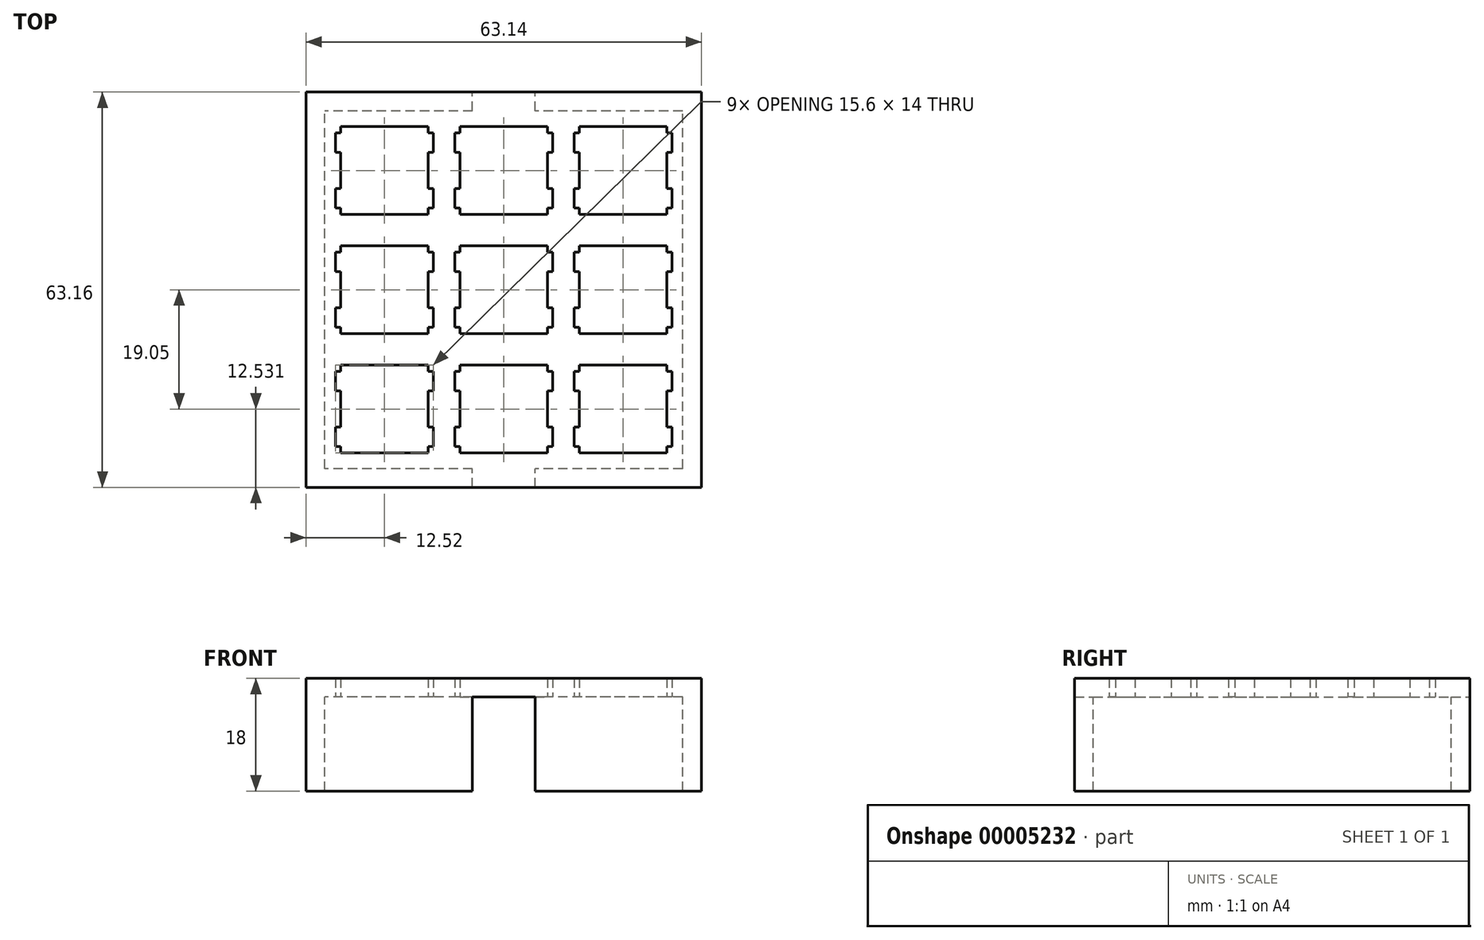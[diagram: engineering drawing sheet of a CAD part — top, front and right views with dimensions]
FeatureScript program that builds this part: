
annotation { "Feature Type Name" : "Feature", "Feature Type Description" : "" }
export const myFeature = defineFeature(function(context is Context, id is Id, definition is map)
    precondition{}
    {
        {
            var Q0;
            Q0=qCreatedBy(makeId("Top.planeOp"),FACE);
            var sketch = newSketch(context, id + "F0", { "sketchPlane" : qUnion([Q0])});
            skLineSegment(sketch, "E0", {"start": v(-31.57, 31.58) * mm, "end": v(31.57, 31.58) * mm});
            skLineSegment(sketch, "E1", {"start": v(31.57, 31.58) * mm, "end": v(31.57, -31.58) * mm});
            skLineSegment(sketch, "E2", {"start": v(31.57, -31.58) * mm, "end": v(-31.57, -31.58) * mm});
            skLineSegment(sketch, "E3", {"start": v(-31.57, -31.58) * mm, "end": v(-31.57, 31.58) * mm});
            skLineSegment(sketch, "E4", {"start": v(-12.05, 13.05) * mm, "end": v(-12.05, 12.05) * mm});
            skLineSegment(sketch, "E5", {"start": v(-12.05, 12.05) * mm, "end": v(-26.05, 12.05) * mm});
            skLineSegment(sketch, "E6", {"start": v(-26.05, 12.05) * mm, "end": v(-26.05, 13.05) * mm});
            skLineSegment(sketch, "E7", {"start": v(-26.05, 13.05) * mm, "end": v(-26.85, 13.05) * mm});
            skLineSegment(sketch, "E8", {"start": v(-26.85, 13.05) * mm, "end": v(-26.85, 16.15) * mm});
            skLineSegment(sketch, "E9", {"start": v(-26.85, 16.15) * mm, "end": v(-26.05, 16.15) * mm});
            skLineSegment(sketch, "E10", {"start": v(-26.05, 16.15) * mm, "end": v(-26.05, 21.95) * mm});
            skLineSegment(sketch, "E11", {"start": v(-26.05, 21.95) * mm, "end": v(-26.85, 21.95) * mm});
            skLineSegment(sketch, "E12", {"start": v(-26.85, 21.95) * mm, "end": v(-26.85, 25.05) * mm});
            skLineSegment(sketch, "E13", {"start": v(-26.85, 25.05) * mm, "end": v(-26.05, 25.05) * mm});
            skLineSegment(sketch, "E14", {"start": v(-26.05, 25.05) * mm, "end": v(-26.05, 26.05) * mm});
            skLineSegment(sketch, "E15", {"start": v(-26.05, 26.05) * mm, "end": v(-12.05, 26.05) * mm});
            skLineSegment(sketch, "E16", {"start": v(-12.05, 26.05) * mm, "end": v(-12.05, 25.05) * mm});
            skLineSegment(sketch, "E17", {"start": v(-12.05, 25.05) * mm, "end": v(-11.25, 25.05) * mm});
            skLineSegment(sketch, "E18", {"start": v(-11.25, 25.05) * mm, "end": v(-11.25, 21.95) * mm});
            skLineSegment(sketch, "E19", {"start": v(-11.25, 21.95) * mm, "end": v(-12.05, 21.95) * mm});
            skLineSegment(sketch, "E20", {"start": v(-12.05, 21.95) * mm, "end": v(-12.05, 16.15) * mm});
            skLineSegment(sketch, "E21", {"start": v(-12.05, 16.15) * mm, "end": v(-11.25, 16.15) * mm});
            skLineSegment(sketch, "E22", {"start": v(-11.25, 16.15) * mm, "end": v(-11.25, 13.05) * mm});
            skLineSegment(sketch, "E23", {"start": v(-11.25, 13.05) * mm, "end": v(-12.05, 13.05) * mm});
            skLineSegment(sketch, "E24", {"start": v(-12.05, -6) * mm, "end": v(-12.05, -7) * mm});
            skLineSegment(sketch, "E25", {"start": v(-12.05, -7) * mm, "end": v(-26.05, -7) * mm});
            skLineSegment(sketch, "E26", {"start": v(-26.05, -7) * mm, "end": v(-26.05, -6) * mm});
            skLineSegment(sketch, "E27", {"start": v(-26.05, -6) * mm, "end": v(-26.85, -6) * mm});
            skLineSegment(sketch, "E28", {"start": v(-26.85, -6) * mm, "end": v(-26.85, -2.9) * mm});
            skLineSegment(sketch, "E29", {"start": v(-26.85, -2.9) * mm, "end": v(-26.05, -2.9) * mm});
            skLineSegment(sketch, "E30", {"start": v(-26.05, -2.9) * mm, "end": v(-26.05, 2.9) * mm});
            skLineSegment(sketch, "E31", {"start": v(-26.05, 2.9) * mm, "end": v(-26.85, 2.9) * mm});
            skLineSegment(sketch, "E32", {"start": v(-26.85, 2.9) * mm, "end": v(-26.85, 6) * mm});
            skLineSegment(sketch, "E33", {"start": v(-26.85, 6) * mm, "end": v(-26.05, 6) * mm});
            skLineSegment(sketch, "E34", {"start": v(-26.05, 6) * mm, "end": v(-26.05, 7) * mm});
            skLineSegment(sketch, "E35", {"start": v(-26.05, 7) * mm, "end": v(-12.05, 7) * mm});
            skLineSegment(sketch, "E36", {"start": v(-12.05, 7) * mm, "end": v(-12.05, 6) * mm});
            skLineSegment(sketch, "E37", {"start": v(-12.05, 6) * mm, "end": v(-11.25, 6) * mm});
            skLineSegment(sketch, "E38", {"start": v(-11.25, 6) * mm, "end": v(-11.25, 2.9) * mm});
            skLineSegment(sketch, "E39", {"start": v(-11.25, 2.9) * mm, "end": v(-12.05, 2.9) * mm});
            skLineSegment(sketch, "E40", {"start": v(-12.05, 2.9) * mm, "end": v(-12.05, -2.9) * mm});
            skLineSegment(sketch, "E41", {"start": v(-12.05, -2.9) * mm, "end": v(-11.25, -2.9) * mm});
            skLineSegment(sketch, "E42", {"start": v(-11.25, -2.9) * mm, "end": v(-11.25, -6) * mm});
            skLineSegment(sketch, "E43", {"start": v(-11.25, -6) * mm, "end": v(-12.05, -6) * mm});
            skLineSegment(sketch, "E44", {"start": v(-12.05, -25.05) * mm, "end": v(-12.05, -26.05) * mm});
            skLineSegment(sketch, "E45", {"start": v(-12.05, -26.05) * mm, "end": v(-26.05, -26.05) * mm});
            skLineSegment(sketch, "E46", {"start": v(-26.05, -26.05) * mm, "end": v(-26.05, -25.05) * mm});
            skLineSegment(sketch, "E47", {"start": v(-26.05, -25.05) * mm, "end": v(-26.85, -25.05) * mm});
            skLineSegment(sketch, "E48", {"start": v(-26.85, -25.05) * mm, "end": v(-26.85, -21.95) * mm});
            skLineSegment(sketch, "E49", {"start": v(-26.85, -21.95) * mm, "end": v(-26.05, -21.95) * mm});
            skLineSegment(sketch, "E50", {"start": v(-26.05, -21.95) * mm, "end": v(-26.05, -16.15) * mm});
            skLineSegment(sketch, "E51", {"start": v(-26.05, -16.15) * mm, "end": v(-26.85, -16.15) * mm});
            skLineSegment(sketch, "E52", {"start": v(-26.85, -16.15) * mm, "end": v(-26.85, -13.05) * mm});
            skLineSegment(sketch, "E53", {"start": v(-26.85, -13.05) * mm, "end": v(-26.05, -13.05) * mm});
            skLineSegment(sketch, "E54", {"start": v(-26.05, -13.05) * mm, "end": v(-26.05, -12.05) * mm});
            skLineSegment(sketch, "E55", {"start": v(-26.05, -12.05) * mm, "end": v(-12.05, -12.05) * mm});
            skLineSegment(sketch, "E56", {"start": v(-12.05, -12.05) * mm, "end": v(-12.05, -13.05) * mm});
            skLineSegment(sketch, "E57", {"start": v(-12.05, -13.05) * mm, "end": v(-11.25, -13.05) * mm});
            skLineSegment(sketch, "E58", {"start": v(-11.25, -13.05) * mm, "end": v(-11.25, -16.15) * mm});
            skLineSegment(sketch, "E59", {"start": v(-11.25, -16.15) * mm, "end": v(-12.05, -16.15) * mm});
            skLineSegment(sketch, "E60", {"start": v(-12.05, -16.15) * mm, "end": v(-12.05, -21.95) * mm});
            skLineSegment(sketch, "E61", {"start": v(-12.05, -21.95) * mm, "end": v(-11.25, -21.95) * mm});
            skLineSegment(sketch, "E62", {"start": v(-11.25, -21.95) * mm, "end": v(-11.25, -25.05) * mm});
            skLineSegment(sketch, "E63", {"start": v(-11.25, -25.05) * mm, "end": v(-12.05, -25.05) * mm});
            skLineSegment(sketch, "E64", {"start": v(7, 13.05) * mm, "end": v(7, 12.05) * mm});
            skLineSegment(sketch, "E65", {"start": v(7, 12.05) * mm, "end": v(-7, 12.05) * mm});
            skLineSegment(sketch, "E66", {"start": v(-7, 12.05) * mm, "end": v(-7, 13.05) * mm});
            skLineSegment(sketch, "E67", {"start": v(-7, 13.05) * mm, "end": v(-7.8, 13.05) * mm});
            skLineSegment(sketch, "E68", {"start": v(-7.8, 13.05) * mm, "end": v(-7.8, 16.15) * mm});
            skLineSegment(sketch, "E69", {"start": v(-7.8, 16.15) * mm, "end": v(-7, 16.15) * mm});
            skLineSegment(sketch, "E70", {"start": v(-7, 16.15) * mm, "end": v(-7, 21.95) * mm});
            skLineSegment(sketch, "E71", {"start": v(-7, 21.95) * mm, "end": v(-7.8, 21.95) * mm});
            skLineSegment(sketch, "E72", {"start": v(-7.8, 21.95) * mm, "end": v(-7.8, 25.05) * mm});
            skLineSegment(sketch, "E73", {"start": v(-7.8, 25.05) * mm, "end": v(-7, 25.05) * mm});
            skLineSegment(sketch, "E74", {"start": v(-7, 25.05) * mm, "end": v(-7, 26.05) * mm});
            skLineSegment(sketch, "E75", {"start": v(-7, 26.05) * mm, "end": v(7, 26.05) * mm});
            skLineSegment(sketch, "E76", {"start": v(7, 26.05) * mm, "end": v(7, 25.05) * mm});
            skLineSegment(sketch, "E77", {"start": v(7, 25.05) * mm, "end": v(7.8, 25.05) * mm});
            skLineSegment(sketch, "E78", {"start": v(7.8, 25.05) * mm, "end": v(7.8, 21.95) * mm});
            skLineSegment(sketch, "E79", {"start": v(7.8, 21.95) * mm, "end": v(7, 21.95) * mm});
            skLineSegment(sketch, "E80", {"start": v(7, 21.95) * mm, "end": v(7, 16.15) * mm});
            skLineSegment(sketch, "E81", {"start": v(7, 16.15) * mm, "end": v(7.8, 16.15) * mm});
            skLineSegment(sketch, "E82", {"start": v(7.8, 16.15) * mm, "end": v(7.8, 13.05) * mm});
            skLineSegment(sketch, "E83", {"start": v(7.8, 13.05) * mm, "end": v(7, 13.05) * mm});
            skLineSegment(sketch, "E84", {"start": v(7, -6) * mm, "end": v(7, -7) * mm});
            skLineSegment(sketch, "E85", {"start": v(7, -7) * mm, "end": v(-7, -7) * mm});
            skLineSegment(sketch, "E86", {"start": v(-7, -7) * mm, "end": v(-7, -6) * mm});
            skLineSegment(sketch, "E87", {"start": v(-7, -6) * mm, "end": v(-7.8, -6) * mm});
            skLineSegment(sketch, "E88", {"start": v(-7.8, -6) * mm, "end": v(-7.8, -2.9) * mm});
            skLineSegment(sketch, "E89", {"start": v(-7.8, -2.9) * mm, "end": v(-7, -2.9) * mm});
            skLineSegment(sketch, "E90", {"start": v(-7, -2.9) * mm, "end": v(-7, 2.9) * mm});
            skLineSegment(sketch, "E91", {"start": v(-7, 2.9) * mm, "end": v(-7.8, 2.9) * mm});
            skLineSegment(sketch, "E92", {"start": v(-7.8, 2.9) * mm, "end": v(-7.8, 6) * mm});
            skLineSegment(sketch, "E93", {"start": v(-7.8, 6) * mm, "end": v(-7, 6) * mm});
            skLineSegment(sketch, "E94", {"start": v(-7, 6) * mm, "end": v(-7, 7) * mm});
            skLineSegment(sketch, "E95", {"start": v(-7, 7) * mm, "end": v(7, 7) * mm});
            skLineSegment(sketch, "E96", {"start": v(7, 7) * mm, "end": v(7, 6) * mm});
            skLineSegment(sketch, "E97", {"start": v(7, 6) * mm, "end": v(7.8, 6) * mm});
            skLineSegment(sketch, "E98", {"start": v(7.8, 6) * mm, "end": v(7.8, 2.9) * mm});
            skLineSegment(sketch, "E99", {"start": v(7.8, 2.9) * mm, "end": v(7, 2.9) * mm});
            skLineSegment(sketch, "E100", {"start": v(7, 2.9) * mm, "end": v(7, -2.9) * mm});
            skLineSegment(sketch, "E101", {"start": v(7, -2.9) * mm, "end": v(7.8, -2.9) * mm});
            skLineSegment(sketch, "E102", {"start": v(7.8, -2.9) * mm, "end": v(7.8, -6) * mm});
            skLineSegment(sketch, "E103", {"start": v(7.8, -6) * mm, "end": v(7, -6) * mm});
            skLineSegment(sketch, "E104", {"start": v(7, -25.05) * mm, "end": v(7, -26.05) * mm});
            skLineSegment(sketch, "E105", {"start": v(7, -26.05) * mm, "end": v(-7, -26.05) * mm});
            skLineSegment(sketch, "E106", {"start": v(-7, -26.05) * mm, "end": v(-7, -25.05) * mm});
            skLineSegment(sketch, "E107", {"start": v(-7, -25.05) * mm, "end": v(-7.8, -25.05) * mm});
            skLineSegment(sketch, "E108", {"start": v(-7.8, -25.05) * mm, "end": v(-7.8, -21.95) * mm});
            skLineSegment(sketch, "E109", {"start": v(-7.8, -21.95) * mm, "end": v(-7, -21.95) * mm});
            skLineSegment(sketch, "E110", {"start": v(-7, -21.95) * mm, "end": v(-7, -16.15) * mm});
            skLineSegment(sketch, "E111", {"start": v(-7, -16.15) * mm, "end": v(-7.8, -16.15) * mm});
            skLineSegment(sketch, "E112", {"start": v(-7.8, -16.15) * mm, "end": v(-7.8, -13.05) * mm});
            skLineSegment(sketch, "E113", {"start": v(-7.8, -13.05) * mm, "end": v(-7, -13.05) * mm});
            skLineSegment(sketch, "E114", {"start": v(-7, -13.05) * mm, "end": v(-7, -12.05) * mm});
            skLineSegment(sketch, "E115", {"start": v(-7, -12.05) * mm, "end": v(7, -12.05) * mm});
            skLineSegment(sketch, "E116", {"start": v(7, -12.05) * mm, "end": v(7, -13.05) * mm});
            skLineSegment(sketch, "E117", {"start": v(7, -13.05) * mm, "end": v(7.8, -13.05) * mm});
            skLineSegment(sketch, "E118", {"start": v(7.8, -13.05) * mm, "end": v(7.8, -16.15) * mm});
            skLineSegment(sketch, "E119", {"start": v(7.8, -16.15) * mm, "end": v(7, -16.15) * mm});
            skLineSegment(sketch, "E120", {"start": v(7, -16.15) * mm, "end": v(7, -21.95) * mm});
            skLineSegment(sketch, "E121", {"start": v(7, -21.95) * mm, "end": v(7.8, -21.95) * mm});
            skLineSegment(sketch, "E122", {"start": v(7.8, -21.95) * mm, "end": v(7.8, -25.05) * mm});
            skLineSegment(sketch, "E123", {"start": v(7.8, -25.05) * mm, "end": v(7, -25.05) * mm});
            skLineSegment(sketch, "E124", {"start": v(26.05, 13.05) * mm, "end": v(26.05, 12.05) * mm});
            skLineSegment(sketch, "E125", {"start": v(26.05, 12.05) * mm, "end": v(12.05, 12.05) * mm});
            skLineSegment(sketch, "E126", {"start": v(12.05, 12.05) * mm, "end": v(12.05, 13.05) * mm});
            skLineSegment(sketch, "E127", {"start": v(12.05, 13.05) * mm, "end": v(11.25, 13.05) * mm});
            skLineSegment(sketch, "E128", {"start": v(11.25, 13.05) * mm, "end": v(11.25, 16.15) * mm});
            skLineSegment(sketch, "E129", {"start": v(11.25, 16.15) * mm, "end": v(12.05, 16.15) * mm});
            skLineSegment(sketch, "E130", {"start": v(12.05, 16.15) * mm, "end": v(12.05, 21.95) * mm});
            skLineSegment(sketch, "E131", {"start": v(12.05, 21.95) * mm, "end": v(11.25, 21.95) * mm});
            skLineSegment(sketch, "E132", {"start": v(11.25, 21.95) * mm, "end": v(11.25, 25.05) * mm});
            skLineSegment(sketch, "E133", {"start": v(11.25, 25.05) * mm, "end": v(12.05, 25.05) * mm});
            skLineSegment(sketch, "E134", {"start": v(12.05, 25.05) * mm, "end": v(12.05, 26.05) * mm});
            skLineSegment(sketch, "E135", {"start": v(12.05, 26.05) * mm, "end": v(26.05, 26.05) * mm});
            skLineSegment(sketch, "E136", {"start": v(26.05, 26.05) * mm, "end": v(26.05, 25.05) * mm});
            skLineSegment(sketch, "E137", {"start": v(26.05, 25.05) * mm, "end": v(26.85, 25.05) * mm});
            skLineSegment(sketch, "E138", {"start": v(26.85, 25.05) * mm, "end": v(26.85, 21.95) * mm});
            skLineSegment(sketch, "E139", {"start": v(26.85, 21.95) * mm, "end": v(26.05, 21.95) * mm});
            skLineSegment(sketch, "E140", {"start": v(26.05, 21.95) * mm, "end": v(26.05, 16.15) * mm});
            skLineSegment(sketch, "E141", {"start": v(26.05, 16.15) * mm, "end": v(26.85, 16.15) * mm});
            skLineSegment(sketch, "E142", {"start": v(26.85, 16.15) * mm, "end": v(26.85, 13.05) * mm});
            skLineSegment(sketch, "E143", {"start": v(26.85, 13.05) * mm, "end": v(26.05, 13.05) * mm});
            skLineSegment(sketch, "E144", {"start": v(26.05, -6) * mm, "end": v(26.05, -7) * mm});
            skLineSegment(sketch, "E145", {"start": v(26.05, -7) * mm, "end": v(12.05, -7) * mm});
            skLineSegment(sketch, "E146", {"start": v(12.05, -7) * mm, "end": v(12.05, -6) * mm});
            skLineSegment(sketch, "E147", {"start": v(12.05, -6) * mm, "end": v(11.25, -6) * mm});
            skLineSegment(sketch, "E148", {"start": v(11.25, -6) * mm, "end": v(11.25, -2.9) * mm});
            skLineSegment(sketch, "E149", {"start": v(11.25, -2.9) * mm, "end": v(12.05, -2.9) * mm});
            skLineSegment(sketch, "E150", {"start": v(12.05, -2.9) * mm, "end": v(12.05, 2.9) * mm});
            skLineSegment(sketch, "E151", {"start": v(12.05, 2.9) * mm, "end": v(11.25, 2.9) * mm});
            skLineSegment(sketch, "E152", {"start": v(11.25, 2.9) * mm, "end": v(11.25, 6) * mm});
            skLineSegment(sketch, "E153", {"start": v(11.25, 6) * mm, "end": v(12.05, 6) * mm});
            skLineSegment(sketch, "E154", {"start": v(12.05, 6) * mm, "end": v(12.05, 7) * mm});
            skLineSegment(sketch, "E155", {"start": v(12.05, 7) * mm, "end": v(26.05, 7) * mm});
            skLineSegment(sketch, "E156", {"start": v(26.05, 7) * mm, "end": v(26.05, 6) * mm});
            skLineSegment(sketch, "E157", {"start": v(26.05, 6) * mm, "end": v(26.85, 6) * mm});
            skLineSegment(sketch, "E158", {"start": v(26.85, 6) * mm, "end": v(26.85, 2.9) * mm});
            skLineSegment(sketch, "E159", {"start": v(26.85, 2.9) * mm, "end": v(26.05, 2.9) * mm});
            skLineSegment(sketch, "E160", {"start": v(26.05, 2.9) * mm, "end": v(26.05, -2.9) * mm});
            skLineSegment(sketch, "E161", {"start": v(26.05, -2.9) * mm, "end": v(26.85, -2.9) * mm});
            skLineSegment(sketch, "E162", {"start": v(26.85, -2.9) * mm, "end": v(26.85, -6) * mm});
            skLineSegment(sketch, "E163", {"start": v(26.85, -6) * mm, "end": v(26.05, -6) * mm});
            skLineSegment(sketch, "E164", {"start": v(26.05, -25.05) * mm, "end": v(26.05, -26.05) * mm});
            skLineSegment(sketch, "E165", {"start": v(26.05, -26.05) * mm, "end": v(12.05, -26.05) * mm});
            skLineSegment(sketch, "E166", {"start": v(12.05, -26.05) * mm, "end": v(12.05, -25.05) * mm});
            skLineSegment(sketch, "E167", {"start": v(12.05, -25.05) * mm, "end": v(11.25, -25.05) * mm});
            skLineSegment(sketch, "E168", {"start": v(11.25, -25.05) * mm, "end": v(11.25, -21.95) * mm});
            skLineSegment(sketch, "E169", {"start": v(11.25, -21.95) * mm, "end": v(12.05, -21.95) * mm});
            skLineSegment(sketch, "E170", {"start": v(12.05, -21.95) * mm, "end": v(12.05, -16.15) * mm});
            skLineSegment(sketch, "E171", {"start": v(12.05, -16.15) * mm, "end": v(11.25, -16.15) * mm});
            skLineSegment(sketch, "E172", {"start": v(11.25, -16.15) * mm, "end": v(11.25, -13.05) * mm});
            skLineSegment(sketch, "E173", {"start": v(11.25, -13.05) * mm, "end": v(12.05, -13.05) * mm});
            skLineSegment(sketch, "E174", {"start": v(12.05, -13.05) * mm, "end": v(12.05, -12.05) * mm});
            skLineSegment(sketch, "E175", {"start": v(12.05, -12.05) * mm, "end": v(26.05, -12.05) * mm});
            skLineSegment(sketch, "E176", {"start": v(26.05, -12.05) * mm, "end": v(26.05, -13.05) * mm});
            skLineSegment(sketch, "E177", {"start": v(26.05, -13.05) * mm, "end": v(26.85, -13.05) * mm});
            skLineSegment(sketch, "E178", {"start": v(26.85, -13.05) * mm, "end": v(26.85, -16.15) * mm});
            skLineSegment(sketch, "E179", {"start": v(26.85, -16.15) * mm, "end": v(26.05, -16.15) * mm});
            skLineSegment(sketch, "E180", {"start": v(26.05, -16.15) * mm, "end": v(26.05, -21.95) * mm});
            skLineSegment(sketch, "E181", {"start": v(26.05, -21.95) * mm, "end": v(26.85, -21.95) * mm});
            skLineSegment(sketch, "E182", {"start": v(26.85, -21.95) * mm, "end": v(26.85, -25.05) * mm});
            skLineSegment(sketch, "E183", {"start": v(26.85, -25.05) * mm, "end": v(26.05, -25.05) * mm});
            skSolve(sketch);
        }
        {
            var Q0;
            Q0 = qSketchRegion(id + "F0", true);
            extrude(context, id + "F1", {"entities" : qUnion([Q0]), "depth" : 3 * mm});
        }
        {
            var Q0;
            Q0=makeQuery(id+"F1.opExtrude","CAP_FACE",FACE,{"disambiguationData":[OSD([sQuery(id+"F0.wireOp",EDGE,"E0"),sQuery(id+"F0.wireOp",EDGE,"E1"),sQuery(id+"F0.wireOp",EDGE,"E2"),sQuery(id+"F0.wireOp",EDGE,"E3"),sQuery(id+"F0.wireOp",EDGE,"E4"),sQuery(id+"F0.wireOp",EDGE,"E5"),sQuery(id+"F0.wireOp",EDGE,"E6"),sQuery(id+"F0.wireOp",EDGE,"E7"),sQuery(id+"F0.wireOp",EDGE,"E8"),sQuery(id+"F0.wireOp",EDGE,"E9"),sQuery(id+"F0.wireOp",EDGE,"E10"),sQuery(id+"F0.wireOp",EDGE,"E11"),sQuery(id+"F0.wireOp",EDGE,"E12"),sQuery(id+"F0.wireOp",EDGE,"E13"),sQuery(id+"F0.wireOp",EDGE,"E14"),sQuery(id+"F0.wireOp",EDGE,"E15"),sQuery(id+"F0.wireOp",EDGE,"E16"),sQuery(id+"F0.wireOp",EDGE,"E17"),sQuery(id+"F0.wireOp",EDGE,"E18"),sQuery(id+"F0.wireOp",EDGE,"E19"),sQuery(id+"F0.wireOp",EDGE,"E20"),sQuery(id+"F0.wireOp",EDGE,"E21"),sQuery(id+"F0.wireOp",EDGE,"E22"),sQuery(id+"F0.wireOp",EDGE,"E23"),sQuery(id+"F0.wireOp",EDGE,"E24"),sQuery(id+"F0.wireOp",EDGE,"E25"),sQuery(id+"F0.wireOp",EDGE,"E26"),sQuery(id+"F0.wireOp",EDGE,"E27"),sQuery(id+"F0.wireOp",EDGE,"E28"),sQuery(id+"F0.wireOp",EDGE,"E29"),sQuery(id+"F0.wireOp",EDGE,"E30"),sQuery(id+"F0.wireOp",EDGE,"E31"),sQuery(id+"F0.wireOp",EDGE,"E32"),sQuery(id+"F0.wireOp",EDGE,"E33"),sQuery(id+"F0.wireOp",EDGE,"E34"),sQuery(id+"F0.wireOp",EDGE,"E35"),sQuery(id+"F0.wireOp",EDGE,"E36"),sQuery(id+"F0.wireOp",EDGE,"E37"),sQuery(id+"F0.wireOp",EDGE,"E38"),sQuery(id+"F0.wireOp",EDGE,"E39"),sQuery(id+"F0.wireOp",EDGE,"E40"),sQuery(id+"F0.wireOp",EDGE,"E41"),sQuery(id+"F0.wireOp",EDGE,"E42"),sQuery(id+"F0.wireOp",EDGE,"E43"),sQuery(id+"F0.wireOp",EDGE,"E44"),sQuery(id+"F0.wireOp",EDGE,"E45"),sQuery(id+"F0.wireOp",EDGE,"E46"),sQuery(id+"F0.wireOp",EDGE,"E47"),sQuery(id+"F0.wireOp",EDGE,"E48"),sQuery(id+"F0.wireOp",EDGE,"E49"),sQuery(id+"F0.wireOp",EDGE,"E50"),sQuery(id+"F0.wireOp",EDGE,"E51"),sQuery(id+"F0.wireOp",EDGE,"E52"),sQuery(id+"F0.wireOp",EDGE,"E53"),sQuery(id+"F0.wireOp",EDGE,"E54"),sQuery(id+"F0.wireOp",EDGE,"E55"),sQuery(id+"F0.wireOp",EDGE,"E56"),sQuery(id+"F0.wireOp",EDGE,"E57"),sQuery(id+"F0.wireOp",EDGE,"E58"),sQuery(id+"F0.wireOp",EDGE,"E59"),sQuery(id+"F0.wireOp",EDGE,"E60"),sQuery(id+"F0.wireOp",EDGE,"E61"),sQuery(id+"F0.wireOp",EDGE,"E62"),sQuery(id+"F0.wireOp",EDGE,"E63"),sQuery(id+"F0.wireOp",EDGE,"E64"),sQuery(id+"F0.wireOp",EDGE,"E65"),sQuery(id+"F0.wireOp",EDGE,"E66"),sQuery(id+"F0.wireOp",EDGE,"E67"),sQuery(id+"F0.wireOp",EDGE,"E68"),sQuery(id+"F0.wireOp",EDGE,"E69"),sQuery(id+"F0.wireOp",EDGE,"E70"),sQuery(id+"F0.wireOp",EDGE,"E71"),sQuery(id+"F0.wireOp",EDGE,"E72"),sQuery(id+"F0.wireOp",EDGE,"E73"),sQuery(id+"F0.wireOp",EDGE,"E74"),sQuery(id+"F0.wireOp",EDGE,"E75"),sQuery(id+"F0.wireOp",EDGE,"E76"),sQuery(id+"F0.wireOp",EDGE,"E77"),sQuery(id+"F0.wireOp",EDGE,"E78"),sQuery(id+"F0.wireOp",EDGE,"E79"),sQuery(id+"F0.wireOp",EDGE,"E80"),sQuery(id+"F0.wireOp",EDGE,"E81"),sQuery(id+"F0.wireOp",EDGE,"E82"),sQuery(id+"F0.wireOp",EDGE,"E83"),sQuery(id+"F0.wireOp",EDGE,"E84"),sQuery(id+"F0.wireOp",EDGE,"E85"),sQuery(id+"F0.wireOp",EDGE,"E86"),sQuery(id+"F0.wireOp",EDGE,"E87"),sQuery(id+"F0.wireOp",EDGE,"E88"),sQuery(id+"F0.wireOp",EDGE,"E89"),sQuery(id+"F0.wireOp",EDGE,"E90"),sQuery(id+"F0.wireOp",EDGE,"E91"),sQuery(id+"F0.wireOp",EDGE,"E92"),sQuery(id+"F0.wireOp",EDGE,"E93"),sQuery(id+"F0.wireOp",EDGE,"E94"),sQuery(id+"F0.wireOp",EDGE,"E95"),sQuery(id+"F0.wireOp",EDGE,"E96"),sQuery(id+"F0.wireOp",EDGE,"E97"),sQuery(id+"F0.wireOp",EDGE,"E98"),sQuery(id+"F0.wireOp",EDGE,"E99"),sQuery(id+"F0.wireOp",EDGE,"E100"),sQuery(id+"F0.wireOp",EDGE,"E101"),sQuery(id+"F0.wireOp",EDGE,"E102"),sQuery(id+"F0.wireOp",EDGE,"E103"),sQuery(id+"F0.wireOp",EDGE,"E104"),sQuery(id+"F0.wireOp",EDGE,"E105"),sQuery(id+"F0.wireOp",EDGE,"E106"),sQuery(id+"F0.wireOp",EDGE,"E107"),sQuery(id+"F0.wireOp",EDGE,"E108"),sQuery(id+"F0.wireOp",EDGE,"E109"),sQuery(id+"F0.wireOp",EDGE,"E110"),sQuery(id+"F0.wireOp",EDGE,"E111"),sQuery(id+"F0.wireOp",EDGE,"E112"),sQuery(id+"F0.wireOp",EDGE,"E113"),sQuery(id+"F0.wireOp",EDGE,"E114"),sQuery(id+"F0.wireOp",EDGE,"E115"),sQuery(id+"F0.wireOp",EDGE,"E116"),sQuery(id+"F0.wireOp",EDGE,"E117"),sQuery(id+"F0.wireOp",EDGE,"E118"),sQuery(id+"F0.wireOp",EDGE,"E119"),sQuery(id+"F0.wireOp",EDGE,"E120"),sQuery(id+"F0.wireOp",EDGE,"E121"),sQuery(id+"F0.wireOp",EDGE,"E122"),sQuery(id+"F0.wireOp",EDGE,"E123"),sQuery(id+"F0.wireOp",EDGE,"E124"),sQuery(id+"F0.wireOp",EDGE,"E125"),sQuery(id+"F0.wireOp",EDGE,"E126"),sQuery(id+"F0.wireOp",EDGE,"E127"),sQuery(id+"F0.wireOp",EDGE,"E128"),sQuery(id+"F0.wireOp",EDGE,"E129"),sQuery(id+"F0.wireOp",EDGE,"E130"),sQuery(id+"F0.wireOp",EDGE,"E131"),sQuery(id+"F0.wireOp",EDGE,"E132"),sQuery(id+"F0.wireOp",EDGE,"E133"),sQuery(id+"F0.wireOp",EDGE,"E134"),sQuery(id+"F0.wireOp",EDGE,"E135"),sQuery(id+"F0.wireOp",EDGE,"E136"),sQuery(id+"F0.wireOp",EDGE,"E137"),sQuery(id+"F0.wireOp",EDGE,"E138"),sQuery(id+"F0.wireOp",EDGE,"E139"),sQuery(id+"F0.wireOp",EDGE,"E140"),sQuery(id+"F0.wireOp",EDGE,"E141"),sQuery(id+"F0.wireOp",EDGE,"E142"),sQuery(id+"F0.wireOp",EDGE,"E143"),sQuery(id+"F0.wireOp",EDGE,"E144"),sQuery(id+"F0.wireOp",EDGE,"E145"),sQuery(id+"F0.wireOp",EDGE,"E146"),sQuery(id+"F0.wireOp",EDGE,"E147"),sQuery(id+"F0.wireOp",EDGE,"E148"),sQuery(id+"F0.wireOp",EDGE,"E149"),sQuery(id+"F0.wireOp",EDGE,"E150"),sQuery(id+"F0.wireOp",EDGE,"E151"),sQuery(id+"F0.wireOp",EDGE,"E152"),sQuery(id+"F0.wireOp",EDGE,"E153"),sQuery(id+"F0.wireOp",EDGE,"E154"),sQuery(id+"F0.wireOp",EDGE,"E155"),sQuery(id+"F0.wireOp",EDGE,"E156"),sQuery(id+"F0.wireOp",EDGE,"E157"),sQuery(id+"F0.wireOp",EDGE,"E158"),sQuery(id+"F0.wireOp",EDGE,"E159"),sQuery(id+"F0.wireOp",EDGE,"E160"),sQuery(id+"F0.wireOp",EDGE,"E161"),sQuery(id+"F0.wireOp",EDGE,"E162"),sQuery(id+"F0.wireOp",EDGE,"E163"),sQuery(id+"F0.wireOp",EDGE,"E164"),sQuery(id+"F0.wireOp",EDGE,"E165"),sQuery(id+"F0.wireOp",EDGE,"E166"),sQuery(id+"F0.wireOp",EDGE,"E167"),sQuery(id+"F0.wireOp",EDGE,"E168"),sQuery(id+"F0.wireOp",EDGE,"E169"),sQuery(id+"F0.wireOp",EDGE,"E170"),sQuery(id+"F0.wireOp",EDGE,"E171"),sQuery(id+"F0.wireOp",EDGE,"E172"),sQuery(id+"F0.wireOp",EDGE,"E173"),sQuery(id+"F0.wireOp",EDGE,"E174"),sQuery(id+"F0.wireOp",EDGE,"E175"),sQuery(id+"F0.wireOp",EDGE,"E176"),sQuery(id+"F0.wireOp",EDGE,"E177"),sQuery(id+"F0.wireOp",EDGE,"E178"),sQuery(id+"F0.wireOp",EDGE,"E179"),sQuery(id+"F0.wireOp",EDGE,"E180"),sQuery(id+"F0.wireOp",EDGE,"E181"),sQuery(id+"F0.wireOp",EDGE,"E182"),sQuery(id+"F0.wireOp",EDGE,"E183")])],"isStart":true});
            var sketch = newSketch(context, id + "F2", { "sketchPlane" : qUnion([Q0])});
            skLineSegment(sketch, "E184.0", {"start": v(31.57, 31.58) * mm, "end": v(-31.57, 31.58) * mm});
            skLineSegment(sketch, "E184.1", {"start": v(-31.57, 31.58) * mm, "end": v(-31.57, -31.58) * mm});
            skLineSegment(sketch, "E184.2", {"start": v(31.57, -31.58) * mm, "end": v(31.57, 31.58) * mm});
            skLineSegment(sketch, "E184.3", {"start": v(-31.57, -31.58) * mm, "end": v(31.57, -31.58) * mm});
            skLineSegment(sketch, "E185.bottom", {"start": v(28.57, 28.58) * mm, "end": v(-28.57, 28.58) * mm});
            skLineSegment(sketch, "E185.top", {"start": v(28.57, -28.58) * mm, "end": v(-28.57, -28.58) * mm});
            skLineSegment(sketch, "E185.left", {"start": v(28.57, 28.58) * mm, "end": v(28.57, -28.58) * mm});
            skLineSegment(sketch, "E185.right", {"start": v(-28.57, 28.58) * mm, "end": v(-28.57, -28.58) * mm});
            skPoint(sketch, "E185.middle", {"position": v(0, 0) * mm});
            skSolve(sketch);
        }
        {
            var Q0;
            Q0 = qSketchRegion(id + "F2", true);
            extrude(context, id + "F3", {"entities" : qUnion([Q0]), "operationType" : NewBodyOperationType.ADD, "depth" : 15 * mm});
        }
        {
            var Q0;
            Q0=makeQuery(id+"F3.opExtrude","CAP_FACE",FACE,{"disambiguationData":[OSD([sQuery(id+"F2.wireOp",EDGE,"E184.0"),sQuery(id+"F2.wireOp",EDGE,"E184.1"),sQuery(id+"F2.wireOp",EDGE,"E184.2"),sQuery(id+"F2.wireOp",EDGE,"E184.3"),sQuery(id+"F2.wireOp",EDGE,"E185.bottom"),sQuery(id+"F2.wireOp",EDGE,"E185.top"),sQuery(id+"F2.wireOp",EDGE,"E185.left"),sQuery(id+"F2.wireOp",EDGE,"E185.right")])],"isStart":false});
            var sketch = newSketch(context, id + "F4", { "sketchPlane" : qUnion([Q0])});
            skLineSegment(sketch, "E186", {"start": v(0, 0) * mm, "end": v(31.57, 0) * mm, "construction": true});
            skLineSegment(sketch, "E187.bottom", {"start": v(-5, 31.58) * mm, "end": v(5, 31.58) * mm});
            skLineSegment(sketch, "E187.top", {"start": v(-5, -31.58) * mm, "end": v(5, -31.58) * mm});
            skLineSegment(sketch, "E187.left", {"start": v(-5, 31.58) * mm, "end": v(-5, -31.58) * mm});
            skLineSegment(sketch, "E187.right", {"start": v(5, 31.58) * mm, "end": v(5, -31.58) * mm});
            skLineSegment(sketch, "E188", {"start": v(0, 0) * mm, "end": v(0, -20.27) * mm, "construction": true});
            skSolve(sketch);
        }
        {
            var Q0;
            Q0 = qSketchRegion(id + "F4", true);
            var Q1;
            Q1=makeQuery(id+"F1.opExtrude","CAP_FACE",FACE,{"disambiguationData":[OSD([sQuery(id+"F0.wireOp",EDGE,"E0"),sQuery(id+"F0.wireOp",EDGE,"E1"),sQuery(id+"F0.wireOp",EDGE,"E2"),sQuery(id+"F0.wireOp",EDGE,"E3"),sQuery(id+"F0.wireOp",EDGE,"E4"),sQuery(id+"F0.wireOp",EDGE,"E5"),sQuery(id+"F0.wireOp",EDGE,"E6"),sQuery(id+"F0.wireOp",EDGE,"E7"),sQuery(id+"F0.wireOp",EDGE,"E8"),sQuery(id+"F0.wireOp",EDGE,"E9"),sQuery(id+"F0.wireOp",EDGE,"E10"),sQuery(id+"F0.wireOp",EDGE,"E11"),sQuery(id+"F0.wireOp",EDGE,"E12"),sQuery(id+"F0.wireOp",EDGE,"E13"),sQuery(id+"F0.wireOp",EDGE,"E14"),sQuery(id+"F0.wireOp",EDGE,"E15"),sQuery(id+"F0.wireOp",EDGE,"E16"),sQuery(id+"F0.wireOp",EDGE,"E17"),sQuery(id+"F0.wireOp",EDGE,"E18"),sQuery(id+"F0.wireOp",EDGE,"E19"),sQuery(id+"F0.wireOp",EDGE,"E20"),sQuery(id+"F0.wireOp",EDGE,"E21"),sQuery(id+"F0.wireOp",EDGE,"E22"),sQuery(id+"F0.wireOp",EDGE,"E23"),sQuery(id+"F0.wireOp",EDGE,"E24"),sQuery(id+"F0.wireOp",EDGE,"E25"),sQuery(id+"F0.wireOp",EDGE,"E26"),sQuery(id+"F0.wireOp",EDGE,"E27"),sQuery(id+"F0.wireOp",EDGE,"E28"),sQuery(id+"F0.wireOp",EDGE,"E29"),sQuery(id+"F0.wireOp",EDGE,"E30"),sQuery(id+"F0.wireOp",EDGE,"E31"),sQuery(id+"F0.wireOp",EDGE,"E32"),sQuery(id+"F0.wireOp",EDGE,"E33"),sQuery(id+"F0.wireOp",EDGE,"E34"),sQuery(id+"F0.wireOp",EDGE,"E35"),sQuery(id+"F0.wireOp",EDGE,"E36"),sQuery(id+"F0.wireOp",EDGE,"E37"),sQuery(id+"F0.wireOp",EDGE,"E38"),sQuery(id+"F0.wireOp",EDGE,"E39"),sQuery(id+"F0.wireOp",EDGE,"E40"),sQuery(id+"F0.wireOp",EDGE,"E41"),sQuery(id+"F0.wireOp",EDGE,"E42"),sQuery(id+"F0.wireOp",EDGE,"E43"),sQuery(id+"F0.wireOp",EDGE,"E44"),sQuery(id+"F0.wireOp",EDGE,"E45"),sQuery(id+"F0.wireOp",EDGE,"E46"),sQuery(id+"F0.wireOp",EDGE,"E47"),sQuery(id+"F0.wireOp",EDGE,"E48"),sQuery(id+"F0.wireOp",EDGE,"E49"),sQuery(id+"F0.wireOp",EDGE,"E50"),sQuery(id+"F0.wireOp",EDGE,"E51"),sQuery(id+"F0.wireOp",EDGE,"E52"),sQuery(id+"F0.wireOp",EDGE,"E53"),sQuery(id+"F0.wireOp",EDGE,"E54"),sQuery(id+"F0.wireOp",EDGE,"E55"),sQuery(id+"F0.wireOp",EDGE,"E56"),sQuery(id+"F0.wireOp",EDGE,"E57"),sQuery(id+"F0.wireOp",EDGE,"E58"),sQuery(id+"F0.wireOp",EDGE,"E59"),sQuery(id+"F0.wireOp",EDGE,"E60"),sQuery(id+"F0.wireOp",EDGE,"E61"),sQuery(id+"F0.wireOp",EDGE,"E62"),sQuery(id+"F0.wireOp",EDGE,"E63"),sQuery(id+"F0.wireOp",EDGE,"E64"),sQuery(id+"F0.wireOp",EDGE,"E65"),sQuery(id+"F0.wireOp",EDGE,"E66"),sQuery(id+"F0.wireOp",EDGE,"E67"),sQuery(id+"F0.wireOp",EDGE,"E68"),sQuery(id+"F0.wireOp",EDGE,"E69"),sQuery(id+"F0.wireOp",EDGE,"E70"),sQuery(id+"F0.wireOp",EDGE,"E71"),sQuery(id+"F0.wireOp",EDGE,"E72"),sQuery(id+"F0.wireOp",EDGE,"E73"),sQuery(id+"F0.wireOp",EDGE,"E74"),sQuery(id+"F0.wireOp",EDGE,"E75"),sQuery(id+"F0.wireOp",EDGE,"E76"),sQuery(id+"F0.wireOp",EDGE,"E77"),sQuery(id+"F0.wireOp",EDGE,"E78"),sQuery(id+"F0.wireOp",EDGE,"E79"),sQuery(id+"F0.wireOp",EDGE,"E80"),sQuery(id+"F0.wireOp",EDGE,"E81"),sQuery(id+"F0.wireOp",EDGE,"E82"),sQuery(id+"F0.wireOp",EDGE,"E83"),sQuery(id+"F0.wireOp",EDGE,"E84"),sQuery(id+"F0.wireOp",EDGE,"E85"),sQuery(id+"F0.wireOp",EDGE,"E86"),sQuery(id+"F0.wireOp",EDGE,"E87"),sQuery(id+"F0.wireOp",EDGE,"E88"),sQuery(id+"F0.wireOp",EDGE,"E89"),sQuery(id+"F0.wireOp",EDGE,"E90"),sQuery(id+"F0.wireOp",EDGE,"E91"),sQuery(id+"F0.wireOp",EDGE,"E92"),sQuery(id+"F0.wireOp",EDGE,"E93"),sQuery(id+"F0.wireOp",EDGE,"E94"),sQuery(id+"F0.wireOp",EDGE,"E95"),sQuery(id+"F0.wireOp",EDGE,"E96"),sQuery(id+"F0.wireOp",EDGE,"E97"),sQuery(id+"F0.wireOp",EDGE,"E98"),sQuery(id+"F0.wireOp",EDGE,"E99"),sQuery(id+"F0.wireOp",EDGE,"E100"),sQuery(id+"F0.wireOp",EDGE,"E101"),sQuery(id+"F0.wireOp",EDGE,"E102"),sQuery(id+"F0.wireOp",EDGE,"E103"),sQuery(id+"F0.wireOp",EDGE,"E104"),sQuery(id+"F0.wireOp",EDGE,"E105"),sQuery(id+"F0.wireOp",EDGE,"E106"),sQuery(id+"F0.wireOp",EDGE,"E107"),sQuery(id+"F0.wireOp",EDGE,"E108"),sQuery(id+"F0.wireOp",EDGE,"E109"),sQuery(id+"F0.wireOp",EDGE,"E110"),sQuery(id+"F0.wireOp",EDGE,"E111"),sQuery(id+"F0.wireOp",EDGE,"E112"),sQuery(id+"F0.wireOp",EDGE,"E113"),sQuery(id+"F0.wireOp",EDGE,"E114"),sQuery(id+"F0.wireOp",EDGE,"E115"),sQuery(id+"F0.wireOp",EDGE,"E116"),sQuery(id+"F0.wireOp",EDGE,"E117"),sQuery(id+"F0.wireOp",EDGE,"E118"),sQuery(id+"F0.wireOp",EDGE,"E119"),sQuery(id+"F0.wireOp",EDGE,"E120"),sQuery(id+"F0.wireOp",EDGE,"E121"),sQuery(id+"F0.wireOp",EDGE,"E122"),sQuery(id+"F0.wireOp",EDGE,"E123"),sQuery(id+"F0.wireOp",EDGE,"E124"),sQuery(id+"F0.wireOp",EDGE,"E125"),sQuery(id+"F0.wireOp",EDGE,"E126"),sQuery(id+"F0.wireOp",EDGE,"E127"),sQuery(id+"F0.wireOp",EDGE,"E128"),sQuery(id+"F0.wireOp",EDGE,"E129"),sQuery(id+"F0.wireOp",EDGE,"E130"),sQuery(id+"F0.wireOp",EDGE,"E131"),sQuery(id+"F0.wireOp",EDGE,"E132"),sQuery(id+"F0.wireOp",EDGE,"E133"),sQuery(id+"F0.wireOp",EDGE,"E134"),sQuery(id+"F0.wireOp",EDGE,"E135"),sQuery(id+"F0.wireOp",EDGE,"E136"),sQuery(id+"F0.wireOp",EDGE,"E137"),sQuery(id+"F0.wireOp",EDGE,"E138"),sQuery(id+"F0.wireOp",EDGE,"E139"),sQuery(id+"F0.wireOp",EDGE,"E140"),sQuery(id+"F0.wireOp",EDGE,"E141"),sQuery(id+"F0.wireOp",EDGE,"E142"),sQuery(id+"F0.wireOp",EDGE,"E143"),sQuery(id+"F0.wireOp",EDGE,"E144"),sQuery(id+"F0.wireOp",EDGE,"E145"),sQuery(id+"F0.wireOp",EDGE,"E146"),sQuery(id+"F0.wireOp",EDGE,"E147"),sQuery(id+"F0.wireOp",EDGE,"E148"),sQuery(id+"F0.wireOp",EDGE,"E149"),sQuery(id+"F0.wireOp",EDGE,"E150"),sQuery(id+"F0.wireOp",EDGE,"E151"),sQuery(id+"F0.wireOp",EDGE,"E152"),sQuery(id+"F0.wireOp",EDGE,"E153"),sQuery(id+"F0.wireOp",EDGE,"E154"),sQuery(id+"F0.wireOp",EDGE,"E155"),sQuery(id+"F0.wireOp",EDGE,"E156"),sQuery(id+"F0.wireOp",EDGE,"E157"),sQuery(id+"F0.wireOp",EDGE,"E158"),sQuery(id+"F0.wireOp",EDGE,"E159"),sQuery(id+"F0.wireOp",EDGE,"E160"),sQuery(id+"F0.wireOp",EDGE,"E161"),sQuery(id+"F0.wireOp",EDGE,"E162"),sQuery(id+"F0.wireOp",EDGE,"E163"),sQuery(id+"F0.wireOp",EDGE,"E164"),sQuery(id+"F0.wireOp",EDGE,"E165"),sQuery(id+"F0.wireOp",EDGE,"E166"),sQuery(id+"F0.wireOp",EDGE,"E167"),sQuery(id+"F0.wireOp",EDGE,"E168"),sQuery(id+"F0.wireOp",EDGE,"E169"),sQuery(id+"F0.wireOp",EDGE,"E170"),sQuery(id+"F0.wireOp",EDGE,"E171"),sQuery(id+"F0.wireOp",EDGE,"E172"),sQuery(id+"F0.wireOp",EDGE,"E173"),sQuery(id+"F0.wireOp",EDGE,"E174"),sQuery(id+"F0.wireOp",EDGE,"E175"),sQuery(id+"F0.wireOp",EDGE,"E176"),sQuery(id+"F0.wireOp",EDGE,"E177"),sQuery(id+"F0.wireOp",EDGE,"E178"),sQuery(id+"F0.wireOp",EDGE,"E179"),sQuery(id+"F0.wireOp",EDGE,"E180"),sQuery(id+"F0.wireOp",EDGE,"E181"),sQuery(id+"F0.wireOp",EDGE,"E182"),sQuery(id+"F0.wireOp",EDGE,"E183")])],"isStart":true});
            extrude(context, id + "F5", {"entities" : qUnion([Q0]), "operationType" : NewBodyOperationType.REMOVE, "endBound" : BoundingType.UP_TO_SURFACE, "oppositeDirection" : true, "endBoundEntityFace" : qUnion([Q1]), "depth" : 25 * mm});
        }
    });
